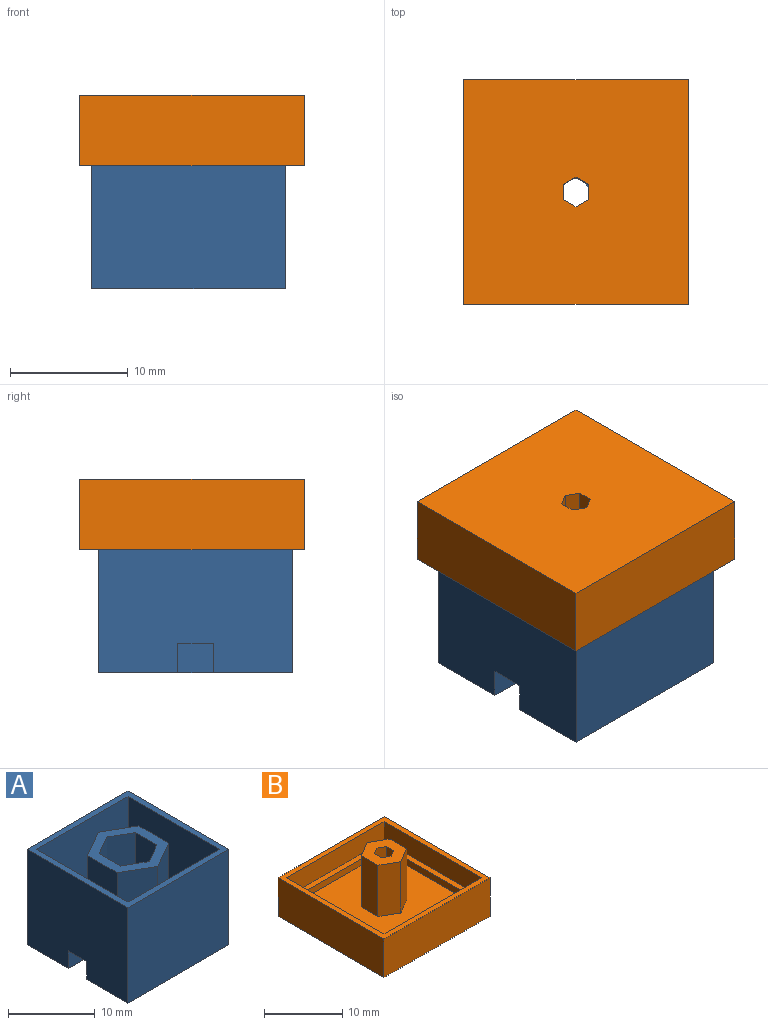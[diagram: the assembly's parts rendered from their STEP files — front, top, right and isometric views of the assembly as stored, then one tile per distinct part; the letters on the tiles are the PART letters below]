
ASSEMBLY  parts=2 mates=1
PART A: 34 faces, bbox 16.5x16.5x13.5 mm
  f0: plane 14.9x14.9mm, normal (0,0,1), area 160.9mm2, adj f19,f20,f21,f22,f23,f24,f29,f30
  f1: plane 4x2.5mm, normal (0,-1,0), area 10mm2, adj f2,f4,f13,f27
  f2: plane 3x2.5mm, normal (-1,0,0), area 7.5mm2, adj f1,f3,f13,f27
  f3: plane 4x2.5mm, normal (0,1,0), area 10mm2, adj f2,f4,f13,f27
  f4: plane 16.5x13.5mm, normal (-1,0,0), area 215.2mm2, adj f1,f3,f5,f11,f13,f27,f33
  f5: plane 16.5x13.5mm, normal (0,-1,0), area 222.7mm2, adj f4,f9,f13,f33
  f6: plane 4x2.5mm, normal (0,1,0), area 10mm2, adj f7,f9,f13,f28
  f7: plane 3x2.5mm, normal (1,0,0), area 7.5mm2, adj f6,f8,f13,f28
  f8: plane 4x2.5mm, normal (0,-1,0), area 10mm2, adj f7,f9,f13,f28
  f9: plane 16.5x13.5mm, normal (1,0,0), area 215.2mm2, adj f5,f6,f8,f11,f13,f28,f33
  f10: cylinder r=1.5mm len=3mm, axis (0,0,-1), area 23.6mm2, adj f12,f13
  f11: plane 16.5x13.5mm, normal (0,1,0), area 222.7mm2, adj f4,f9,f13,f33
  f12: plane 6.93x6mm, normal (0,0,1), area 24.1mm2, adj f10,f14,f15,f16,f17,f18,f25
  f13: plane 16.5x16.5mm, normal (0,0,-1), area 241.2mm2, adj f1,f2,f3,f4,f5,f6,f7,f8
  f14: plane 11x3mm, normal (0.5,0.87,0), area 38.1mm2, adj f12,f15,f25,f26
  f15: plane 11x3.46mm, normal (1,0,0), area 38.1mm2, adj f12,f14,f16,f26
  f16: plane 11x3mm, normal (0.5,-0.87,0), area 38.1mm2, adj f12,f15,f17,f26
  f17: plane 11x3mm, normal (-0.5,-0.87,0), area 38.1mm2, adj f12,f16,f18,f26
  f18: plane 11x3.46mm, normal (-1,0,0), area 38.1mm2, adj f12,f17,f25,f26
  f19: plane 9x4.85mm, normal (1,0,0), area 43.6mm2, adj f0,f20,f24,f26
  f20: plane 9x4.2mm, normal (0.5,0.87,0), area 43.6mm2, adj f0,f19,f21,f26
  f21: plane 9x4.2mm, normal (-0.5,0.87,0), area 43.6mm2, adj f0,f20,f22,f26
  f22: plane 9x4.85mm, normal (-1,0,0), area 43.6mm2, adj f0,f21,f23,f26
  f23: plane 9x4.2mm, normal (-0.5,-0.87,0), area 43.6mm2, adj f0,f22,f24,f26
  f24: plane 9x4.2mm, normal (0.5,-0.87,0), area 43.6mm2, adj f0,f19,f23,f26
  f25: plane 11x3mm, normal (-0.5,0.87,0), area 38.1mm2, adj f12,f14,f18,f26
  f26: plane 9.7x8.4mm, normal (0,0,1), area 29.9mm2, adj f14,f15,f16,f17,f18,f19,f20,f21
  f27: plane 4x3mm, normal (0,0,-1), area 12mm2, adj f1,f2,f3,f4
  f28: plane 4x3mm, normal (0,0,-1), area 12mm2, adj f6,f7,f8,f9
  f29: plane 14.9x9mm, normal (0,-1,0), area 134.1mm2, adj f0,f30,f32,f33
  f30: plane 14.9x9mm, normal (-1,0,0), area 134.1mm2, adj f0,f29,f31,f33
  f31: plane 14.9x9mm, normal (0,1,0), area 134.1mm2, adj f0,f30,f32,f33
  f32: plane 14.9x9mm, normal (1,0,0), area 134.1mm2, adj f0,f29,f31,f33
  f33: plane 16.5x16.5mm, normal (0,0,1), area 50.2mm2, adj f4,f5,f9,f11,f29,f30,f31,f32
PART B: 29 faces, bbox 19.1x19.1x10 mm
  f0: plane 15.9x15.9mm, normal (0,0,1), area 229.4mm2, adj f7,f8,f9,f10,f11,f12,f15,f16
  f1: plane 19.1x19.1mm, normal (0,0,-1), area 360.6mm2, adj f2,f3,f4,f5,f6,f13,f24,f25
  f2: plane 10x1.1mm, normal (-0.5,-0.87,0), area 12.7mm2, adj f1,f3,f13,f14
  f3: plane 10x1.27mm, normal (-1,0,0), area 12.7mm2, adj f1,f2,f4,f14
  f4: plane 10x1.1mm, normal (-0.5,0.87,0), area 12.7mm2, adj f1,f3,f5,f14
  f5: plane 10x1.1mm, normal (0.5,0.87,0), area 12.7mm2, adj f1,f4,f6,f14
  f6: plane 10x1.27mm, normal (1,0,0), area 12.7mm2, adj f1,f5,f13,f14
  f7: plane 8x3mm, normal (1,0,0), area 24mm2, adj f0,f8,f12,f14
  f8: plane 8x2.6mm, normal (0.5,0.87,0), area 24mm2, adj f0,f7,f9,f14
  f9: plane 8x2.6mm, normal (-0.5,0.87,0), area 24mm2, adj f0,f8,f10,f14
  f10: plane 8x3mm, normal (-1,0,0), area 24mm2, adj f0,f9,f11,f14
  f11: plane 8x2.6mm, normal (-0.5,-0.87,0), area 24mm2, adj f0,f10,f12,f14
  f12: plane 8x2.6mm, normal (0.5,-0.87,0), area 24mm2, adj f0,f7,f11,f14
  f13: plane 10x1.1mm, normal (0.5,-0.87,0), area 12.7mm2, adj f1,f2,f6,f14
  f14: plane 6x5.2mm, normal (0,0,1), area 19.2mm2, adj f2,f3,f4,f5,f6,f7,f8,f9
  f15: plane 15.9x1mm, normal (0,1,0), area 15.9mm2, adj f0,f16,f18,f19
  f16: plane 15.9x1mm, normal (-1,0,0), area 15.9mm2, adj f0,f15,f17,f19
  f17: plane 15.9x1mm, normal (0,-1,0), area 15.9mm2, adj f0,f16,f18,f19
  f18: plane 15.9x1mm, normal (1,0,0), area 15.9mm2, adj f0,f15,f17,f19
  f19: plane 17.5x17.5mm, normal (0,0,1), area 53.4mm2, adj f15,f16,f17,f18,f20,f21,f22,f23
  f20: plane 17.5x3mm, normal (1,0,0), area 52.5mm2, adj f19,f21,f23,f28
  f21: plane 17.5x3mm, normal (0,1,0), area 52.5mm2, adj f19,f20,f22,f28
  f22: plane 17.5x3mm, normal (-1,0,0), area 52.5mm2, adj f19,f21,f23,f28
  f23: plane 17.5x3mm, normal (0,-1,0), area 52.5mm2, adj f19,f20,f22,f28
  f24: plane 19.1x6mm, normal (0,-1,0), area 114.6mm2, adj f1,f25,f27,f28
  f25: plane 19.1x6mm, normal (1,0,0), area 114.6mm2, adj f1,f24,f26,f28
  f26: plane 19.1x6mm, normal (0,1,0), area 114.6mm2, adj f1,f25,f27,f28
  f27: plane 19.1x6mm, normal (-1,0,0), area 114.6mm2, adj f1,f24,f26,f28
  f28: plane 19.1x19.1mm, normal (0,0,1), area 58.6mm2, adj f20,f21,f22,f23,f24,f25,f26,f27
PLACE A t=(-13.38,0.63,-2.01)mm
PLACE B rot(axis=(0,1,0),180deg) t=(7.67,0.93,14.49)mm
MATE fastened B.f19 <-> A.f33  axis (0,0,-1) through (-5.13,8.88,11.49)mm
